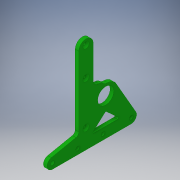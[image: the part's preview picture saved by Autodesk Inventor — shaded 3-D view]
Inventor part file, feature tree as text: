
AUTODESK INVENTOR PART (.ipt)
format: ipt  version: 2018 (Build 220112000, 112)  size: 194,048 bytes
history: native  units: in
note: dims shown in document units (in); Inventor stores cm internally (conversion verified against a paired STEP export)
features: extrude x2, chamfer x1, fillet x1, sketch x1, projected_geometry x1
ambient origin geometry x8: Origin, YZ Plane, XZ Plane, XY Plane, X Axis, Y Axis, Z Axis, Center Point
bodies: Solid1 (feature_tree)
feature tree (6):
  extrude  "Extrusion1"  Depth=5.0in
  chamfer  "Chamfer1"  Distance=0.5in
  extrude  "Extrusion2"  Depth=1.0in
  fillet  "Fillet1"  Radius=0.375in
  sketch  "Sketch2"  dims[d0=0.196in d1=5.0in d3=0.5in d13=1.0in d14=0.375in d18=0.25in d19=0.0in d20=0.375in d30=0.125in d31=0.125in d32=45.0deg d33=1.125in d34=1.0in d35=1.75in d37=3.0in d38=2.725in d39=0.875in d40=0.375in d42=0.4566in d45=0.264in d46=0.467in d47=0.264in d52=1.763in d53=1.7631in d54=1.9739in d55=2.345in d56=0.25in d57=0.0in d58=0.25in d60=2.47in d62=0.625in d63=0.375in d64=0.375in d65=1.0in d66=0.0in d67=1.0in d68=0.0625in]
  projected_geometry  "Projected Loop1"
